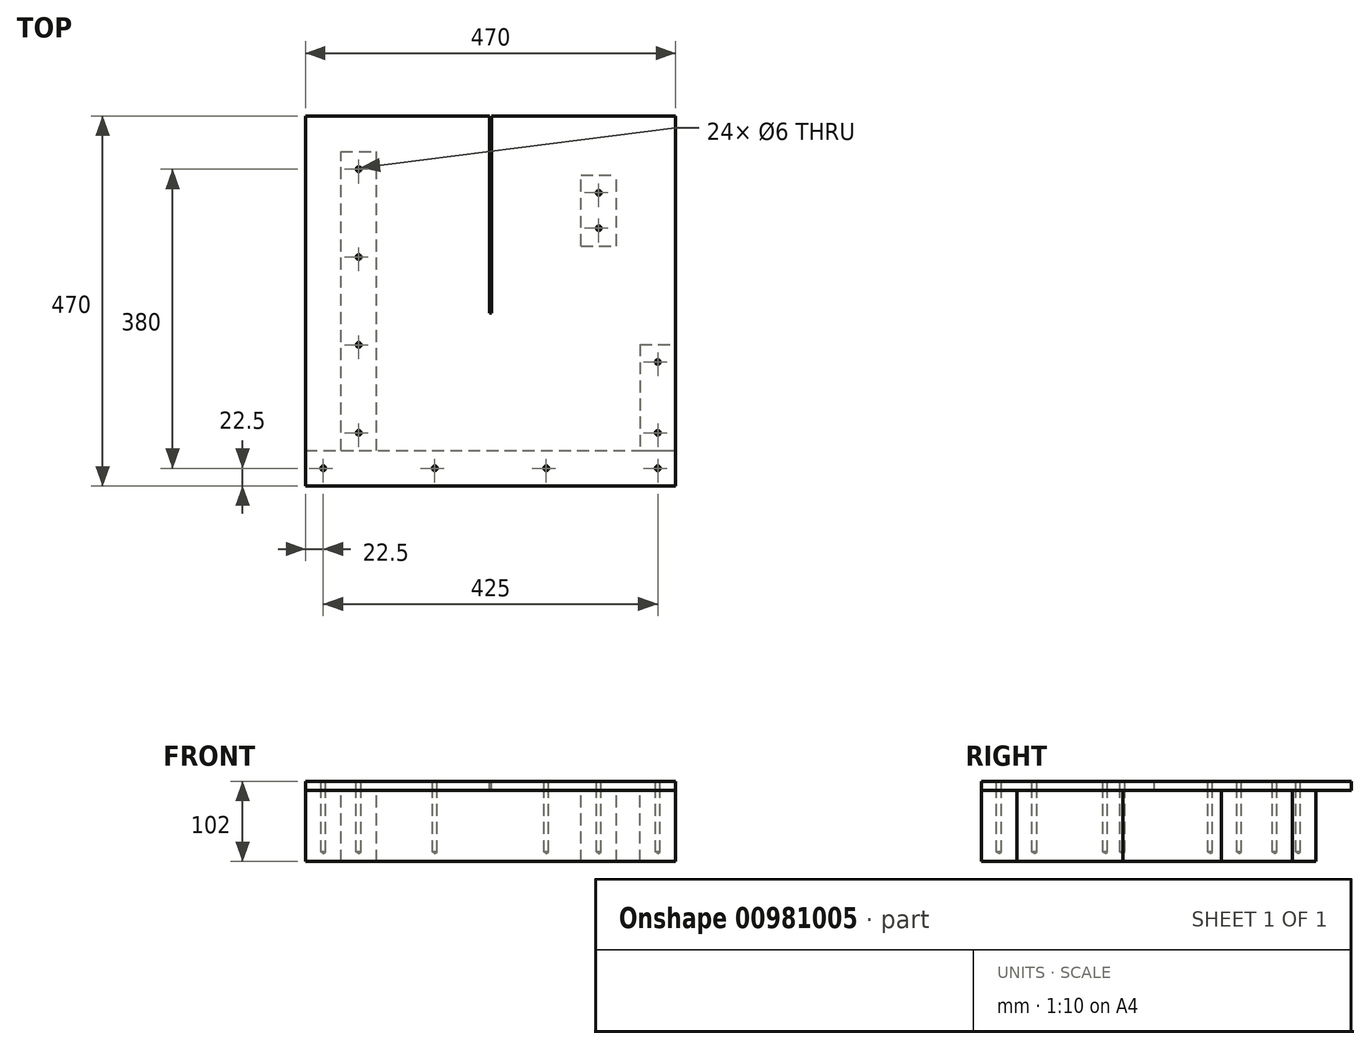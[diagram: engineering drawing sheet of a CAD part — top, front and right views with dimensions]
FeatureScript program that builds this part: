
annotation { "Feature Type Name" : "Feature", "Feature Type Description" : "" }
export const myFeature = defineFeature(function(context is Context, id is Id, definition is map)
    precondition{}
    {
        {
            var Q0;
            Q0=qCreatedBy(makeId("Top.planeOp"),FACE);
            var sketch = newSketch(context, id + "F0", { "sketchPlane" : qUnion([Q0])});
            skLineSegment(sketch, "E0.bottom", {"start": v(235, -235) * mm, "end": v(-235, -235) * mm});
            skLineSegment(sketch, "E0.top", {"start": v(235, 235) * mm, "end": v(-235, 235) * mm});
            skLineSegment(sketch, "E0.left", {"start": v(235, -235) * mm, "end": v(235, 235) * mm});
            skLineSegment(sketch, "E0.right", {"start": v(-235, -235) * mm, "end": v(-235, 235) * mm});
            skPoint(sketch, "E0.middle", {"position": v(0, 0) * mm});
            skSolve(sketch);
        }
        {
            var Q0;
            Q0 = qSketchRegion(id + "F0", true);
            extrude(context, id + "F1", {"entities" : qUnion([Q0]), "depth" : 12 * mm, "offsetDistance" : 25 * mm});
        }
        {
            var Q0;
            Q0=makeQuery(id+"F1.opExtrude","CAP_FACE",FACE,{"disambiguationData":[OSD([sQuery(id+"F0.wireOp",EDGE,"E0.bottom"),sQuery(id+"F0.wireOp",EDGE,"E0.top"),sQuery(id+"F0.wireOp",EDGE,"E0.left"),sQuery(id+"F0.wireOp",EDGE,"E0.right")])],"isStart":true});
            var sketch = newSketch(context, id + "F2", { "sketchPlane" : qUnion([Q0])});
            skLineSegment(sketch, "E1.bottom", {"start": v(-235, 235) * mm, "end": v(235, 235) * mm});
            skLineSegment(sketch, "E1.top", {"start": v(-235, 190) * mm, "end": v(235, 190) * mm});
            skLineSegment(sketch, "E1.left", {"start": v(-235, 235) * mm, "end": v(-235, 190) * mm});
            skLineSegment(sketch, "E1.right", {"start": v(235, 235) * mm, "end": v(235, 190) * mm});
            skLineSegment(sketch, "E2.bottom", {"start": v(-190, 190) * mm, "end": v(-145, 190) * mm});
            skLineSegment(sketch, "E2.top", {"start": v(-190, -190) * mm, "end": v(-145, -190) * mm});
            skLineSegment(sketch, "E2.left", {"start": v(-190, 190) * mm, "end": v(-190, -190) * mm});
            skLineSegment(sketch, "E2.right", {"start": v(-145, 190) * mm, "end": v(-145, -190) * mm});
            skLineSegment(sketch, "E3.bottom", {"start": v(-190, -190) * mm, "end": v(190, -190) * mm});
            skLineSegment(sketch, "E3.top", {"start": v(-190, -235) * mm, "end": v(190, -235) * mm});
            skLineSegment(sketch, "E3.left", {"start": v(-190, -190) * mm, "end": v(-190, -235) * mm});
            skLineSegment(sketch, "E3.right", {"start": v(190, -190) * mm, "end": v(190, -235) * mm});
            skLineSegment(sketch, "E4.bottom", {"start": v(190, -235) * mm, "end": v(235, -235) * mm});
            skLineSegment(sketch, "E4.top", {"start": v(190, 55) * mm, "end": v(235, 55) * mm});
            skLineSegment(sketch, "E4.left", {"start": v(190, -235) * mm, "end": v(190, 55) * mm});
            skLineSegment(sketch, "E4.right", {"start": v(235, -235) * mm, "end": v(235, 55) * mm});
            skLineSegment(sketch, "E5.top", {"start": v(190, 190) * mm, "end": v(235, 190) * mm});
            skLineSegment(sketch, "E5.left", {"start": v(190, 55) * mm, "end": v(190, 190) * mm});
            skLineSegment(sketch, "E5.right", {"start": v(235, 55) * mm, "end": v(235, 190) * mm});
            skLineSegment(sketch, "E6.bottom", {"start": v(-190, -235) * mm, "end": v(-235, -235) * mm});
            skLineSegment(sketch, "E6.top", {"start": v(-190, -145) * mm, "end": v(-235, -145) * mm});
            skLineSegment(sketch, "E6.left", {"start": v(-190, -235) * mm, "end": v(-190, -145) * mm});
            skLineSegment(sketch, "E6.right", {"start": v(-235, -235) * mm, "end": v(-235, -145) * mm});
            skLineSegment(sketch, "E7.bottom", {"start": v(115, -70) * mm, "end": v(160, -70) * mm});
            skLineSegment(sketch, "E7.top", {"start": v(115, -160) * mm, "end": v(160, -160) * mm});
            skLineSegment(sketch, "E7.left", {"start": v(115, -70) * mm, "end": v(115, -160) * mm});
            skLineSegment(sketch, "E7.right", {"start": v(160, -70) * mm, "end": v(160, -160) * mm});
            skSolve(sketch);
        }
        {
            var Q0;
            Q0=makeQuery(id+"F2.imprint","IMPRINT",FACE,{"disambiguationData":[TD([[makeQuery(id+"F2.imprint","IMPRINT",EDGE,{"derivedFrom":sQuery(id+"F2.wireOp",EDGE,"E1.bottom")}),1.0]])]});
            extrude(context, id + "F3", {"entities" : qUnion([Q0]), "depth" : 90 * mm, "offsetDistance" : 25 * mm});
        }
        {
            var Q0;
            {var subQ1=sQuery(id+"F2.wireOp",EDGE,"E2.top");Q0=makeQuery(id+"F2.imprint","IMPRINT",FACE,{"disambiguationData":[TD([[makeQuery(id+"F2.imprint","IMPRINT",EDGE,{"derivedFrom":subQ1}),1.0]])]});}
            extrude(context, id + "F4", {"entities" : qUnion([Q0]), "depth" : 90 * mm, "offsetDistance" : 25 * mm});
        }
        {
            var Q0;
            Q0=makeQuery(id+"F2.imprint","IMPRINT",FACE,{"disambiguationData":[TD([[makeQuery(id+"F2.imprint","IMPRINT",EDGE,{"derivedFrom":sQuery(id+"F2.wireOp",EDGE,"E4.top")}),1.0]])]});
            extrude(context, id + "F5", {"entities" : qUnion([Q0]), "depth" : 90 * mm, "offsetDistance" : 25 * mm});
        }
        {
            var Q0;
            Q0=makeQuery(id+"F2.imprint","IMPRINT",FACE,{"disambiguationData":[TD([[makeQuery(id+"F2.imprint","IMPRINT",EDGE,{"derivedFrom":sQuery(id+"F2.wireOp",EDGE,"E7.bottom")}),-1.0]])]});
            extrude(context, id + "F6", {"entities" : qUnion([Q0]), "depth" : 90 * mm, "offsetDistance" : 25 * mm});
        }
        {
            var Q0;
            Q0=makeQuery(id+"F1.opExtrude","CAP_FACE",FACE,{"disambiguationData":[OSD([sQuery(id+"F0.wireOp",EDGE,"E0.bottom"),sQuery(id+"F0.wireOp",EDGE,"E0.top"),sQuery(id+"F0.wireOp",EDGE,"E0.left"),sQuery(id+"F0.wireOp",EDGE,"E0.right")])],"isStart":false});
            var sketch = newSketch(context, id + "F7", { "sketchPlane" : qUnion([Q0])});
            skLineSegment(sketch, "E8.bottom", {"start": v(-1, 235) * mm, "end": v(1, 235) * mm});
            skLineSegment(sketch, "E8.top", {"start": v(-1, -15) * mm, "end": v(1, -15) * mm});
            skLineSegment(sketch, "E8.left", {"start": v(-1, 235) * mm, "end": v(-1, -15) * mm});
            skLineSegment(sketch, "E8.right", {"start": v(1, 235) * mm, "end": v(1, -15) * mm});
            skLineSegment(sketch, "E9", {"start": v(0, -15) * mm, "end": v(0, 0) * mm, "construction": true});
            skSolve(sketch);
        }
        {
            var Q0;
            Q0 = qSketchRegion(id + "F7", true);
            extrude(context, id + "F8", {"entities" : qUnion([Q0]), "operationType" : NewBodyOperationType.REMOVE, "endBound" : BoundingType.THROUGH_ALL, "oppositeDirection" : true, "depth" : 25 * mm, "offsetDistance" : 25 * mm});
        }
        {
            var Q0;
            Q0=makeQuery(id+"F1.opExtrude","CAP_FACE",FACE,{"disambiguationData":[OSD([sQuery(id+"F0.wireOp",EDGE,"E0.bottom"),sQuery(id+"F0.wireOp",EDGE,"E0.top"),sQuery(id+"F0.wireOp",EDGE,"E0.left"),sQuery(id+"F0.wireOp",EDGE,"E0.right")])],"isStart":false});
            var sketch = newSketch(context, id + "F9", { "sketchPlane" : qUnion([Q0])});
            skPoint(sketch, "E10", {"position": v(212.5, -77.5) * mm});
            skPoint(sketch, "E11", {"position": v(212.5, -167.5) * mm});
            skPoint(sketch, "E12", {"position": v(212.5, -212.5) * mm});
            skPoint(sketch, "E13", {"position": v(70.83, -212.5) * mm});
            skPoint(sketch, "E14", {"position": v(-70.83, -212.5) * mm});
            skPoint(sketch, "E15", {"position": v(-212.5, -212.5) * mm});
            skPoint(sketch, "E16", {"position": v(-167.5, -167.5) * mm});
            skPoint(sketch, "E17", {"position": v(-167.5, -55.83) * mm});
            skPoint(sketch, "E18", {"position": v(-167.5, 55.83) * mm});
            skPoint(sketch, "E19", {"position": v(-167.5, 167.5) * mm});
            skPoint(sketch, "E20", {"position": v(137.5, 92.5) * mm});
            skPoint(sketch, "E21", {"position": v(137.5, 137.5) * mm});
            skLineSegment(sketch, "E22", {"start": v(-212.5, -212.5) * mm, "end": v(-70.83, -212.5) * mm, "construction": true});
            skLineSegment(sketch, "E23", {"start": v(70.83, -212.5) * mm, "end": v(-70.83, -212.5) * mm, "construction": true});
            skLineSegment(sketch, "E24", {"start": v(70.83, -212.5) * mm, "end": v(212.5, -212.5) * mm, "construction": true});
            skLineSegment(sketch, "E25", {"start": v(212.5, -167.5) * mm, "end": v(212.5, -77.5) * mm, "construction": true});
            skLineSegment(sketch, "E26", {"start": v(137.5, 92.5) * mm, "end": v(137.5, 137.5) * mm, "construction": true});
            skLineSegment(sketch, "E27", {"start": v(-167.5, 167.5) * mm, "end": v(-167.5, 55.83) * mm, "construction": true});
            skLineSegment(sketch, "E28", {"start": v(-167.5, 55.83) * mm, "end": v(-167.5, -55.83) * mm, "construction": true});
            skLineSegment(sketch, "E29", {"start": v(-167.5, -55.83) * mm, "end": v(-167.5, -167.5) * mm, "construction": true});
            skLineSegment(sketch, "E30", {"start": v(-167.5, 0) * mm, "end": v(-190, 0) * mm, "construction": true});
            skLineSegment(sketch, "E31", {"start": v(0, -212.5) * mm, "end": v(0, -190) * mm, "construction": true});
            skLineSegment(sketch, "E32", {"start": v(212.5, -122.5) * mm, "end": v(190, -122.5) * mm, "construction": true});
            skLineSegment(sketch, "E33", {"start": v(137.5, 115) * mm, "end": v(115, 115) * mm, "construction": true});
            skSolve(sketch);
        }
        {
            var Q0;
            Q0=sQuery(id+"F9.wireOp",VERTEX,"E15");
            var Q1;
            Q1=sQuery(id+"F9.wireOp",VERTEX,"E14");
            var Q2;
            Q2=sQuery(id+"F9.wireOp",VERTEX,"E13");
            var Q3;
            Q3=sQuery(id+"F9.wireOp",VERTEX,"E12");
            var Q4;
            Q4=sQuery(id+"F9.wireOp",VERTEX,"E11");
            var Q5;
            Q5=sQuery(id+"F9.wireOp",VERTEX,"E10");
            var Q6;
            Q6=sQuery(id+"F9.wireOp",VERTEX,"E20");
            var Q7;
            Q7=sQuery(id+"F9.wireOp",VERTEX,"E21");
            var Q8;
            Q8=sQuery(id+"F9.wireOp",VERTEX,"E16");
            var Q9;
            Q9=sQuery(id+"F9.wireOp",VERTEX,"E17");
            var Q10;
            Q10=sQuery(id+"F9.wireOp",VERTEX,"E18");
            var Q11;
            Q11=sQuery(id+"F9.wireOp",VERTEX,"E19");
            var Q12;
            Q12=makeQuery(id+"F1.opExtrude","SWEPT_BODY",BODY,{"disambiguationData":[OSD([sQuery(id+"F0.wireOp",EDGE,"E0.bottom"),sQuery(id+"F0.wireOp",EDGE,"E0.top"),sQuery(id+"F0.wireOp",EDGE,"E0.left"),sQuery(id+"F0.wireOp",EDGE,"E0.right")])]});
            var Q13;
            Q13=makeQuery(id+"F3.opExtrude","SWEPT_BODY",BODY,{"disambiguationData":[OSD([sQuery(id+"F2.wireOp",EDGE,"E1.bottom"),sQuery(id+"F2.wireOp",EDGE,"E1.top"),sQuery(id+"F2.wireOp",EDGE,"E1.left"),sQuery(id+"F2.wireOp",EDGE,"E1.right")])]});
            var Q14;
            Q14=makeQuery(id+"F4.opExtrude","SWEPT_BODY",BODY,{"disambiguationData":[OSD([sQuery(id+"F2.wireOp",EDGE,"E1.top"),sQuery(id+"F2.wireOp",EDGE,"E2.top"),sQuery(id+"F2.wireOp",EDGE,"E2.left"),sQuery(id+"F2.wireOp",EDGE,"E2.right")])]});
            var Q15;
            Q15=makeQuery(id+"F5.opExtrude","SWEPT_BODY",BODY,{"disambiguationData":[OSD([sQuery(id+"F2.wireOp",EDGE,"E1.top"),sQuery(id+"F2.wireOp",EDGE,"E4.top"),sQuery(id+"F2.wireOp",EDGE,"E5.left"),sQuery(id+"F2.wireOp",EDGE,"E5.right")])]});
            var Q16;
            Q16=makeQuery(id+"F6.opExtrude","SWEPT_BODY",BODY,{"disambiguationData":[OSD([sQuery(id+"F2.wireOp",EDGE,"E7.bottom"),sQuery(id+"F2.wireOp",EDGE,"E7.top"),sQuery(id+"F2.wireOp",EDGE,"E7.left"),sQuery(id+"F2.wireOp",EDGE,"E7.right")])]});
            hole(context, id + "F10", {"style" : HoleStyle.SIMPLE, "endStyle" : HoleEndStyle.BLIND, "holeDiameter" : 6 * mm, "majorDiameter" : 5 * mm, "holeDepth" : 90 * mm, "isTappedThrough" : true, "tappedDepth" : 12 * mm, "tapClearance" : 3, "locations" : qUnion([Q0, Q1, Q2, Q3, Q4, Q5, Q6, Q7, Q8, Q9, Q10, Q11]), "scope" : qUnion([Q12, Q13, Q14, Q15, Q16])});
        }
    });
